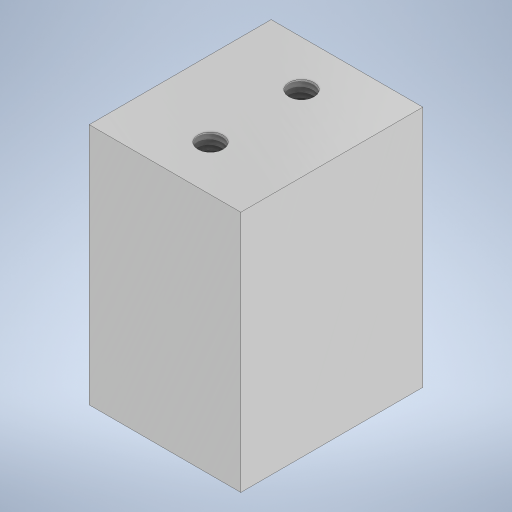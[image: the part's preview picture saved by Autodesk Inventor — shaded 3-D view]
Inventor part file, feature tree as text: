
AUTODESK INVENTOR PART (.ipt)
format: ipt  version: 2023 (Build 270158000, 158)  size: 270,848 bytes
history: native  units: mm
features: sketch x4, extrude x2, hole x2, other x1
ambient origin geometry x8: Origin, YZ Plane, XZ Plane, XY Plane, X Axis, Y Axis, Z Axis, Center Point
bodies: Body1 (feature_tree)
feature tree (9):
  other  "Sólido1"
  extrude  "Extrusão1"  Depth=30.0mm
  hole  "Furo1"  [1 undecoded]
  extrude  "Extrusão2"  Depth=12.5mm
  hole  "Furo3"  [1 undecoded]
  sketch  "Esboço1"  dims[d0=25.0mm d1=30.0mm]
  sketch  "Esboço2"  dims[d2=20.0mm d3=0.0mm d4=25.0mm]
  sketch  "Esboço3"  dims[d5=12.5mm d6=12.5mm]
  sketch  "Esboço5"  dims[d9=4.134mm d10=10.0mm d11=4.0mm d12=2.0mm d13=90.0deg d14=14.2mm d15=20.594885mm d16=25.0mm d17=30.0mm d18=12.5mm d19=15.0mm d21=15.0mm d22=20.0mm d23=0.0mm d31=7.5mm d32=7.5mm d33=8.376mm d34=17.0mm d35=0.624793mm d36=10.589mm d37=4.0mm d38=2.0mm d39=90.0deg d40=20.0mm d41=20.594885mm d24=0.5mm d25=0.872665mm]
note: 2 required parameter values undecoded (feature->parameter linkage not recoverable at this tier; creation-order binding heuristic only, values carry confidence <= 0.55)
